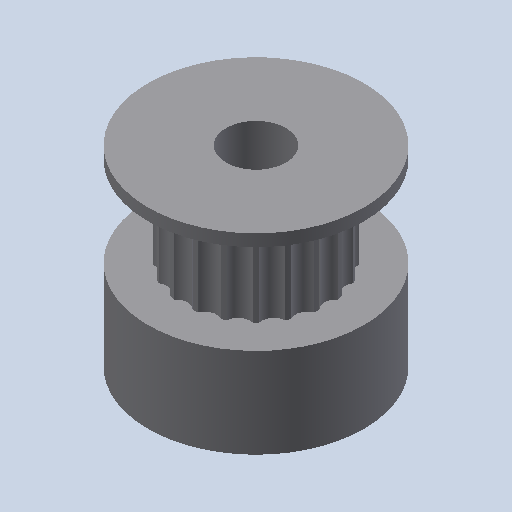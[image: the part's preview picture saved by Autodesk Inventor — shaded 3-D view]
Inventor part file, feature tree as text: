
AUTODESK INVENTOR PART (.ipt)
format: ipt  version: 2022 (Build 260153000, 153)  size: 155,136 bytes
history: native  units: mm
features: sketch x2, revolve x1, extrude x1, pattern_circular x1
ambient origin geometry x8: Origin, YZ Plane, XZ Plane, XY Plane, X Axis, Y Axis, Z Axis, Center Point
bodies: Solid1 (feature_tree)
feature tree (5):
  revolve  "Revolution1"  [1 undecoded]
  extrude  "Extrusion1"  Depth=9.0mm
  pattern_circular  "Circular Pattern1"  [2 undecoded]
  sketch  "Sketch1"  dims[d0=2.5mm d1=7.5mm]
  sketch  "Sketch2"  dims[d2=7.5mm d3=9.0mm d4=1.0mm d6=6.1mm d7=90.0deg d8=2.0mm d9=6.7mm d10=10.0mm d11=0.0mm d12=200.0mm d13=360.0deg]
note: 3 required parameter values undecoded (feature->parameter linkage not recoverable at this tier; creation-order binding heuristic only, values carry confidence <= 0.55)